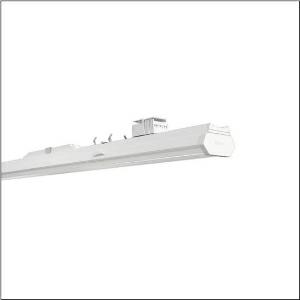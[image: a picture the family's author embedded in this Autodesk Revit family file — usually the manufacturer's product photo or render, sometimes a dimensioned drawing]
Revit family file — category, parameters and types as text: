
# Revit family: licross_21_protected_ho_52tp11cn4c5s
name_source: partatom
category: Lighting Fixtures
units: mm (PartAtom-declared; Revit-internal decimal feet)

## family parameters
Cut with Voids When Loaded = No
Host = Face
Light Source = No
Part Type = Normal
Room Calculation Point = No
Round Connector Dimension = Use Diameter
Shared = No

## types (1)
- --- (1 x LED, 12650 lm, 68.9 W, 4000K)
    Apparent Load = 69 VA
    CIE Flux Codes = 84 94 98 99 100
    Color Rendering = 80
    Color Temperature = 4000K
    Default Elevation = 1800 mm
    Description = Licross 21 Protected HO, luminaire insert, of sheet steel, galvanised, coil coated, white, length: 1.500mm, width: 66mm, height: 67mm, LED rated luminous flux: 12.650lm, light colour: 840, SDCM (Standard Deviation of Colour Matching)MacAdam ≤ 3 SDCM (initial), control gear: ON/OFF Multilumen, CLOi, with plug, 3-pole, with phase selection, mains connection: 220..240V, AC, 50/60Hz, start of lifetime: 69W, end of service life: 83W, internal wiring halogen-free, primary light control with lens, of plastic, primary optical cover: cover, of PMMA, light emission: direct distribution, primary light characteristic: symmetric, protection rating (complete): IP64, insulation class (complete): insulation class I (protective earthing), certification: CE, ENEC, VDE, UKCA, protection symbol: D if used in an environment with conductive dust loads with corresponding accessories, impact resistance: IK06, permissible ambient temperature for indoor applications: -35..+35°C, corresponds to IFS (International Featured Standards) requirements for safety and quality in the food industry, reducing of maximum allowable ambient temperature of 5°C with ceiling mounting, LABS conformity tested according to VDMA 24364:2018-05, The light source and the operating device comply with the requirements of the Ecodesign Regulation (EU) 2019/2020 and are replaceable in accordance with this regulation, packaging unit: 1 piece
    Height = 92 mm
    Lamp = 1 x LED
    Lamp Light Flux = 12650 lm
    Lamp Power = 68.9 W
    Lamp count = 1
    Length = 1500 mm
    Luminous efficacy = 184 lm/W
    Manufacturer = Siteco
    ModVariant = No
    Model = 52TP11CN4C5S
    Mounting Place = Ceiling
    Mounting Type = Pendant
    Number of Poles = 1
    OnlyDefault = Yes
    Power Factor = 1
    Product Name = Licross 21 Protected HO
    Product group = luminaire insert | ceiling pendant
    ProductGroupID = 901
    Protection Class = Protection class I
    Protection Degree = IP 64
    RLX_Detail_Level = 1
    RLX_Emergency_Light_Flux = 0 lm
    RLX_Emergency_Type = 0
    RLX_Emergency_Type_DB = No
    RlxData = <blob elided: 22341 chars, md5=7e4d4052>
    Socket = socket
    Standby Power = 0 W
    System Light Flux = 12650 lm
    System Power = 69 W
    Type Comments = factory setting: luminous flux: 100 % | (A | C | E) | 162 mA
    Type Image = l_1256148.jpg
    URL = http://relux.com
    VarID = @adj_110841
    Voltage = 0 V
    Weight = 0.00 kg
    Width = 88 mm

## geometry (parser evidence)
native form markers: Blend x4, Sweep x10
no freeform markers — native parametric forms only
